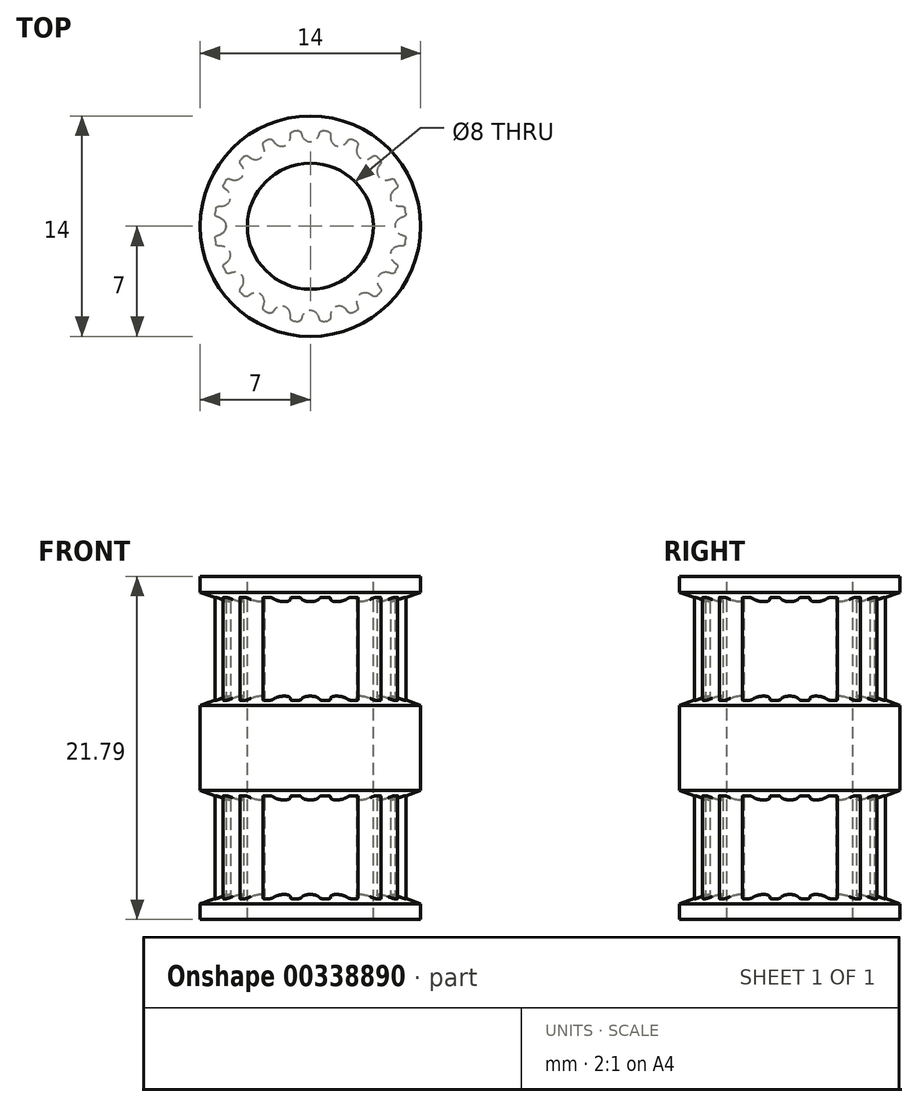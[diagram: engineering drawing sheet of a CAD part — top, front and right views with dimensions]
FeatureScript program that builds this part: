
annotation { "Feature Type Name" : "Feature", "Feature Type Description" : "" }
export const myFeature = defineFeature(function(context is Context, id is Id, definition is map)
    precondition{}
    {
        {
            assignVariable(context, id + "F0", {"name" : "teeth", "anyValue" : 20});
        }
        {
            assignVariable(context, id + "F1", {"name" : "total_length", "anyValue" : 21});
        }
        {
            var Q0;
            Q0=qCreatedBy(makeId("Top.planeOp"),FACE);
            var sketch = newSketch(context, id + "F2", { "sketchPlane" : qUnion([Q0])});
            skLineSegment(sketch, "E0", {"start": v(0, 0) * mm, "end": v(0, 5.36) * mm, "construction": true});
            skCircle(sketch, "E1", {"center": v(0, 0) * mm, "radius": 6.11 * mm});
            skPoint(sketch, "E2.MirrorCS.end.orphan", {"position": v(0.96, 6.04) * mm});
            skLineSegment(sketch, "E3", {"start": v(0.96, 6.04) * mm, "end": v(1, 6.29) * mm, "construction": true});
            skLineSegment(sketch, "E4", {"start": v(-0.96, 6.04) * mm, "end": v(-1, 6.29) * mm, "construction": true});
            skArc(sketch, "E5", {"start": v(0, 5.36) * mm, "mid": v(0.31, 5.46) * mm, "end": v(0.52, 5.72) * mm});
            skArc(sketch, "E6", {"start": v(0.52, 5.72) * mm, "mid": v(0.56, 5.83) * mm, "end": v(0.58, 5.94) * mm, "construction": true});
            skLineSegment(sketch, "E7", {"start": v(0, 5.36) * mm, "end": v(0, 6.11) * mm, "construction": true});
            skLineSegment(sketch, "E8", {"start": v(0, 6.11) * mm, "end": v(0, 6.37) * mm, "construction": true});
            skArc(sketch, "E9", {"start": v(0.58, 5.94) * mm, "mid": v(0.64, 6.04) * mm, "end": v(0.75, 6.07) * mm, "construction": true});
            skArc(sketch, "E10", {"start": v(1, 6.29) * mm, "mid": v(0, 6.37) * mm, "end": v(-1, 6.29) * mm, "construction": true});
            skLineSegment(sketch, "E11", {"start": v(0.96, 6.04) * mm, "end": v(0.84, 5.3) * mm});
            skLineSegment(sketch, "E12", {"start": v(0.84, 5.3) * mm, "end": v(0, 0) * mm});
            skLineSegment(sketch, "E13", {"start": v(0, 0) * mm, "end": v(-0.84, 5.3) * mm});
            skLineSegment(sketch, "E14", {"start": v(-0.84, 5.3) * mm, "end": v(-0.96, 6.04) * mm});
            skArc(sketch, "E15", {"start": v(0.8, 6.06) * mm, "mid": v(0.67, 6.03) * mm, "end": v(0.6, 5.93) * mm});
            skArc(sketch, "E16", {"start": v(0.52, 5.72) * mm, "mid": v(0.56, 5.83) * mm, "end": v(0.6, 5.93) * mm});
            skArc(sketch, "E17.MirrorCS", {"start": v(0, 5.36) * mm, "mid": v(-0.31, 5.46) * mm, "end": v(-0.52, 5.72) * mm});
            skArc(sketch, "E18.MirrorCS", {"start": v(-0.52, 5.72) * mm, "mid": v(-0.56, 5.83) * mm, "end": v(-0.6, 5.93) * mm});
            skArc(sketch, "E19.MirrorCS", {"start": v(-0.8, 6.06) * mm, "mid": v(-0.67, 6.03) * mm, "end": v(-0.6, 5.93) * mm});
            skArc(sketch, "E20", {"start": v(0, 6.11) * mm, "mid": v(-0.2, 6.1) * mm, "end": v(-0.4, 6.1) * mm});
            skArc(sketch, "E21", {"start": v(0.84, 5.3) * mm, "mid": v(0, 5.36) * mm, "end": v(-0.84, 5.3) * mm, "construction": true});
            skLineSegment(sketch, "E22", {"start": v(1, 6.29) * mm, "end": v(1.05, 6.66) * mm, "construction": true});
            skLineSegment(sketch, "E23", {"start": v(-1, 6.29) * mm, "end": v(-1.05, 6.66) * mm, "construction": true});
            skArc(sketch, "E24", {"start": v(-1.05, 6.66) * mm, "mid": v(0, 6.74) * mm, "end": v(1.05, 6.66) * mm, "construction": true});
            skSolve(sketch);
        }
        {
            var Q0;
            Q0=makeQuery(id+"F2.imprint","IMPRINT",FACE,{"disambiguationData":[TD([[makeQuery(id+"F2.imprint","IMPRINT",EDGE,{"derivedFrom":sQuery(id+"F2.wireOp",EDGE,"E5")}),-1.0]])]});
            var Q1;
            {var subQ1=sQuery(id+"F2.wireOp",EDGE,"E14");Q1=makeQuery(id+"F2.imprint","IMPRINT",FACE,{"disambiguationData":[TD([[makeQuery(id+"F2.imprint","IMPRINT",EDGE,{"derivedFrom":subQ1}),-1.0]])]});}
            var Q2;
            {var subQ0=sQuery(id+"F2.wireOp",EDGE,"E12");Q2=makeQuery(id+"F2.imprint","IMPRINT",FACE,{"disambiguationData":[TD([[makeQuery(id+"F2.imprint","IMPRINT",EDGE,{"derivedFrom":subQ0}),-1.0]])]});}
            extrude(context, id + "F3", {"entities" : qUnion([Q0, Q1, Q2]), "endBound" : BoundingType.SYMMETRIC, "depth" : (getVariable(context, 'total_length')) * mm});
        }
        {
            var Q0;
            Q0=makeQuery(id+"F3.opExtrude","SWEPT_BODY",BODY,{"disambiguationData":[OSD([sQuery(id+"F2.wireOp",EDGE,"E1"),sQuery(id+"F2.wireOp",EDGE,"E5"),sQuery(id+"F2.wireOp",EDGE,"E11"),sQuery(id+"F2.wireOp",EDGE,"E12"),sQuery(id+"F2.wireOp",EDGE,"E13"),sQuery(id+"F2.wireOp",EDGE,"E14"),sQuery(id+"F2.wireOp",EDGE,"E15"),sQuery(id+"F2.wireOp",EDGE,"E16"),sQuery(id+"F2.wireOp",EDGE,"E17.MirrorCS"),sQuery(id+"F2.wireOp",EDGE,"E18.MirrorCS"),sQuery(id+"F2.wireOp",EDGE,"E19.MirrorCS")])]});
            var Q1;
            Q1=makeQuery(id+"F3.opExtrude","SWEPT_EDGE",EDGE,{"disambiguationData":[OSD([sQuery(id+"F2.wireOp",EDGE,"E12"),sQuery(id+"F2.wireOp",EDGE,"E13")])]});
            circularPattern(context, id + "F4", {"operationType" : NewBodyOperationType.ADD, "entities" : qUnion([Q0]), "axis" : qUnion([Q1]), "angle" : 360 * degree, "instanceCount" : getVariable(context, 'teeth'), "equalSpace" : true});
        }
        {
            var Q0;
            Q0=qCreatedBy(makeId("Front.planeOp"),FACE);
            var sketch = newSketch(context, id + "F5", { "sketchPlane" : qUnion([Q0])});
            skLineSegment(sketch, "E25", {"start": v(0, 10.5) * mm, "end": v(7, 10.5) * mm});
            skLineSegment(sketch, "E26", {"start": v(7, 10.5) * mm, "end": v(7, 9.5) * mm});
            skLineSegment(sketch, "E27", {"start": v(7, 9.5) * mm, "end": v(5.36, 8.9) * mm});
            skLineSegment(sketch, "E28", {"start": v(5.36, 8.9) * mm, "end": v(0, 8.9) * mm});
            skLineSegment(sketch, "E29", {"start": v(0, 8.9) * mm, "end": v(0, 10.5) * mm});
            skLineSegment(sketch, "E30", {"start": v(0, 2.9) * mm, "end": v(5.36, 2.9) * mm});
            skLineSegment(sketch, "E31", {"start": v(5.36, 2.9) * mm, "end": v(7, 2.3) * mm});
            skLineSegment(sketch, "E32", {"start": v(7, 2.3) * mm, "end": v(7, -3.1) * mm});
            skLineSegment(sketch, "E33", {"start": v(7, -3.1) * mm, "end": v(5.36, -3.7) * mm});
            skLineSegment(sketch, "E34", {"start": v(5.36, -3.7) * mm, "end": v(0, -3.7) * mm});
            skLineSegment(sketch, "E35", {"start": v(0, -3.7) * mm, "end": v(0, 2.9) * mm});
            skLineSegment(sketch, "E36", {"start": v(0, -9.7) * mm, "end": v(5.36, -9.7) * mm});
            skLineSegment(sketch, "E37", {"start": v(5.36, -9.7) * mm, "end": v(7, -10.3) * mm});
            skLineSegment(sketch, "E38", {"start": v(7, -10.3) * mm, "end": v(7, -11.3) * mm});
            skLineSegment(sketch, "E39", {"start": v(7, -11.3) * mm, "end": v(0, -11.3) * mm});
            skLineSegment(sketch, "E40", {"start": v(0, -11.3) * mm, "end": v(0, -9.7) * mm});
            skSolve(sketch);
        }
        {
            var Q0;
            Q0=qSketchRegion(id+"F5",true);
            var Q1;
            Q1=sQuery(id+"F5.wireOp",EDGE,"E35");
            revolve(context, id + "F6", {"operationType" : NewBodyOperationType.ADD, "entities" : qUnion([Q0]), "axis" : qUnion([Q1]), "revolveType" : RevolveType.FULL});
        }
        {
            var Q0;
            Q0=qCreatedBy(makeId("Top.planeOp"),FACE);
            var sketch = newSketch(context, id + "F7", { "sketchPlane" : qUnion([Q0])});
            skCircle(sketch, "E41", {"center": v(0, 0) * mm, "radius": 4 * mm});
            skSolve(sketch);
        }
        {
            var Q0;
            Q0=qSketchRegion(id+"F7",true);
            extrude(context, id + "F8", {"entities" : qUnion([Q0]), "operationType" : NewBodyOperationType.REMOVE, "endBound" : BoundingType.SYMMETRIC, "oppositeDirection" : true, "depth" : 100 * mm});
        }
    });
